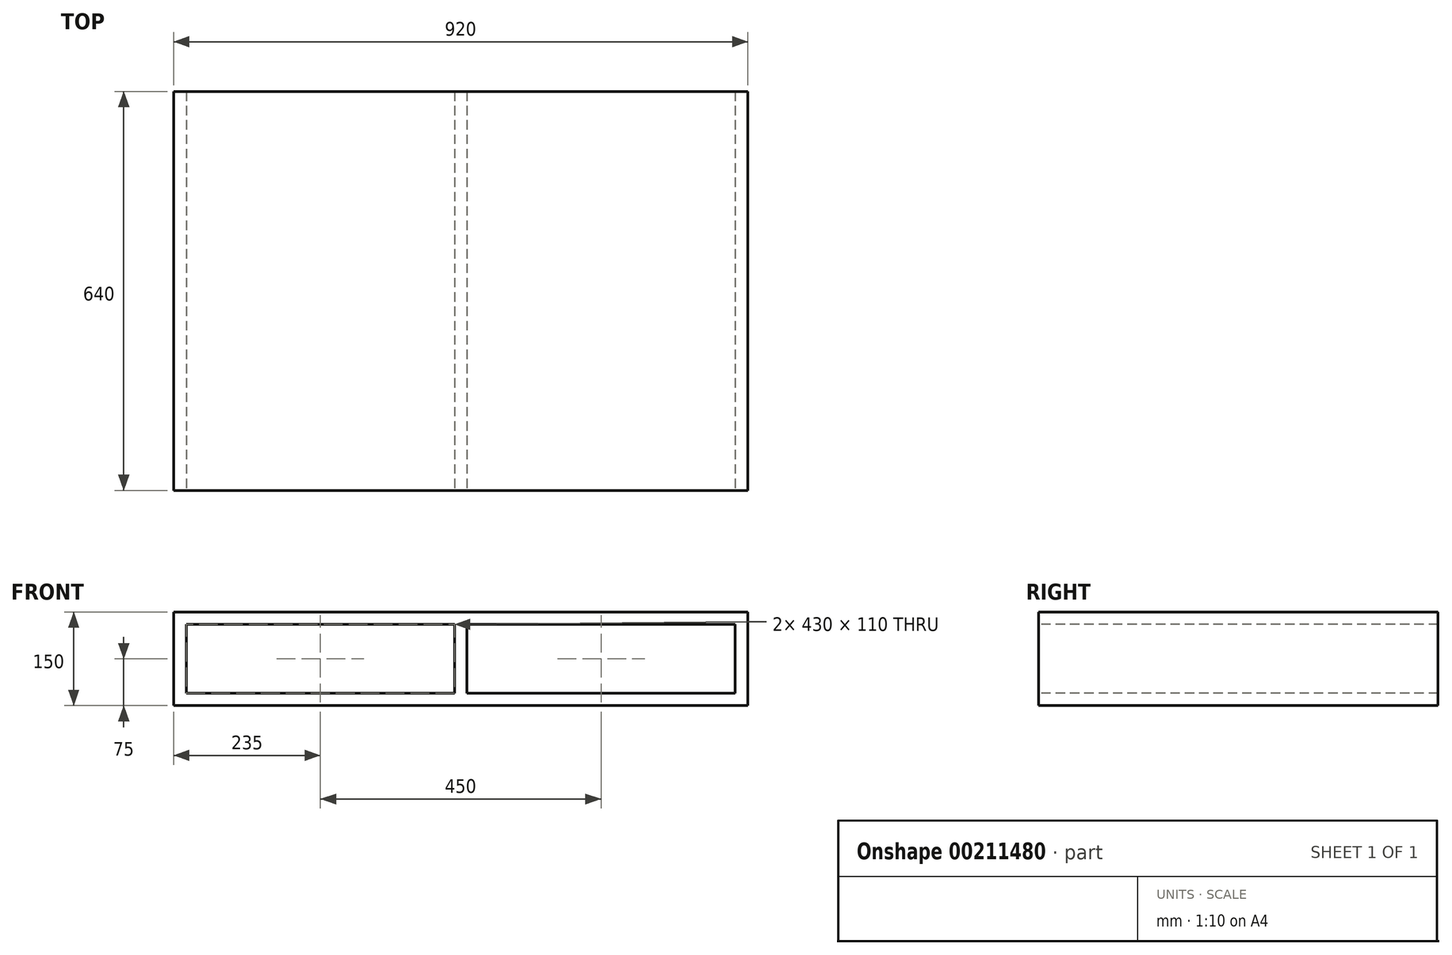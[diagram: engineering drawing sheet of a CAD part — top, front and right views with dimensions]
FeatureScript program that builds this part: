
annotation { "Feature Type Name" : "Feature", "Feature Type Description" : "" }
export const myFeature = defineFeature(function(context is Context, id is Id, definition is map)
    precondition{}
    {
        {
            var Q0;
            Q0=qCreatedBy(makeId("Front.planeOp"),FACE);
            var sketch = newSketch(context, id + "F0", { "sketchPlane" : qUnion([Q0])});
            skLineSegment(sketch, "E0.bottom", {"start": v(460, 75) * mm, "end": v(-460, 75) * mm});
            skLineSegment(sketch, "E0.top", {"start": v(460, -75) * mm, "end": v(-460, -75) * mm});
            skLineSegment(sketch, "E0.left", {"start": v(460, 75) * mm, "end": v(460, -75) * mm});
            skLineSegment(sketch, "E0.right", {"start": v(-460, 75) * mm, "end": v(-460, -75) * mm});
            skPoint(sketch, "E0.middle", {"position": v(0, 0) * mm});
            skSolve(sketch);
        }
        {
            var Q0;
            Q0=makeQuery(id+"F0.imprint","IMPRINT",FACE,{"disambiguationData":[TD([[makeQuery(id+"F0.imprint","IMPRINT",EDGE,{"derivedFrom":sQuery(id+"F0.wireOp",EDGE,"E0.bottom")}),1.0]])]});
            extrude(context, id + "F1", {"entities" : qUnion([Q0]), "depth" : 640 * mm});
        }
        {
            var Q0;
            Q0=makeQuery(id+"F1.opExtrude","CAP_FACE",FACE,{"disambiguationData":[OSD([sQuery(id+"F0.wireOp",EDGE,"E0.bottom"),sQuery(id+"F0.wireOp",EDGE,"E0.top"),sQuery(id+"F0.wireOp",EDGE,"E0.left"),sQuery(id+"F0.wireOp",EDGE,"E0.right")])],"isStart":false});
            var sketch = newSketch(context, id + "F2", { "sketchPlane" : qUnion([Q0])});
            skLineSegment(sketch, "E1", {"start": v(-10, 75) * mm, "end": v(-10, 55) * mm});
            skLineSegment(sketch, "E2.bottom", {"start": v(-10, 55) * mm, "end": v(-440, 55) * mm});
            skLineSegment(sketch, "E2.top", {"start": v(-10, -55) * mm, "end": v(-440, -55) * mm});
            skLineSegment(sketch, "E2.left", {"start": v(-10, 55) * mm, "end": v(-10, -55) * mm});
            skLineSegment(sketch, "E2.right", {"start": v(-440, 55) * mm, "end": v(-440, -55) * mm});
            skLineSegment(sketch, "E3.MirrorCS", {"start": v(10, 55) * mm, "end": v(10, -55) * mm});
            skLineSegment(sketch, "E4.MirrorCS", {"start": v(10, -55) * mm, "end": v(440, -55) * mm});
            skLineSegment(sketch, "E5.MirrorCS", {"start": v(10, 55) * mm, "end": v(440, 55) * mm});
            skLineSegment(sketch, "E6.MirrorCS", {"start": v(440, 55) * mm, "end": v(440, -55) * mm});
            skSolve(sketch);
        }
        {
            var Q0;
            Q0=makeQuery(id+"F2.imprint","IMPRINT",FACE,{"disambiguationData":[TD([[makeQuery(id+"F2.imprint","IMPRINT",EDGE,{"derivedFrom":sQuery(id+"F2.wireOp",EDGE,"E2.bottom")}),1.0]])]});
            var Q1;
            Q1=makeQuery(id+"F2.imprint","IMPRINT",FACE,{"disambiguationData":[TD([[makeQuery(id+"F2.imprint","IMPRINT",EDGE,{"derivedFrom":sQuery(id+"F2.wireOp",EDGE,"E3.MirrorCS")}),1.0]])]});
            extrude(context, id + "F3", {"entities" : qUnion([Q0, Q1]), "operationType" : NewBodyOperationType.REMOVE, "oppositeDirection" : true, "depth" : 650 * mm});
        }
    });
